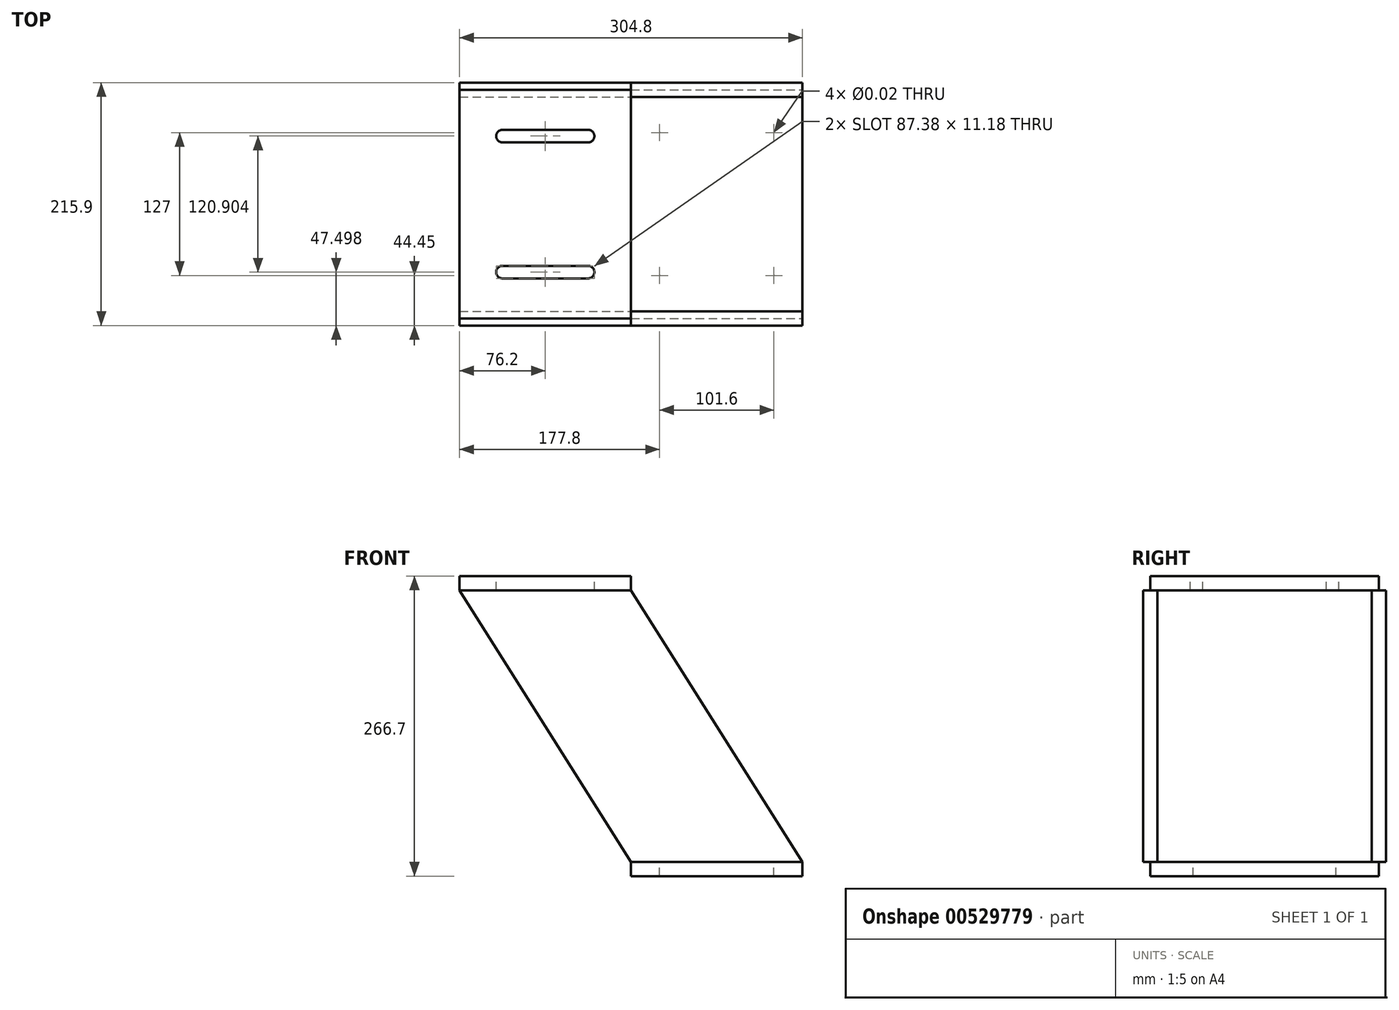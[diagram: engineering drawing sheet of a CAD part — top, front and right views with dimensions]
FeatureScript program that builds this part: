
annotation { "Feature Type Name" : "Feature", "Feature Type Description" : "" }
export const myFeature = defineFeature(function(context is Context, id is Id, definition is map)
    precondition{}
    {
        {
            var Q0;
            Q0=qCreatedBy(makeId("Top.planeOp"),FACE);
            var sketch = newSketch(context, id + "F0", { "sketchPlane" : qUnion([Q0])});
            skLineSegment(sketch, "E0.bottom", {"start": v(-76.2, 101.6) * mm, "end": v(76.2, 101.6) * mm});
            skLineSegment(sketch, "E0.top", {"start": v(-76.2, -101.6) * mm, "end": v(76.2, -101.6) * mm});
            skLineSegment(sketch, "E0.left", {"start": v(-76.2, 101.6) * mm, "end": v(-76.2, -101.6) * mm});
            skLineSegment(sketch, "E0.right", {"start": v(76.2, 101.6) * mm, "end": v(76.2, -101.6) * mm});
            skPoint(sketch, "E0.middle", {"position": v(0, 0) * mm});
            skSolve(sketch);
        }
        {
            var Q0;
            Q0 = qSketchRegion(id + "F0", true);
            extrude(context, id + "F1", {"entities" : qUnion([Q0]), "depth" : 12.7 * mm, "offsetDistance" : 25.4 * mm});
        }
        {
            var Q0;
            Q0=makeQuery(id+"F1.opExtrude","CAP_FACE",FACE,{"disambiguationData":[OSD([sQuery(id+"F0.wireOp",EDGE,"E0.bottom"),sQuery(id+"F0.wireOp",EDGE,"E0.top"),sQuery(id+"F0.wireOp",EDGE,"E0.left"),sQuery(id+"F0.wireOp",EDGE,"E0.right")])],"isStart":false});
            var sketch = newSketch(context, id + "F2", { "sketchPlane" : qUnion([Q0])});
            skLineSegment(sketch, "E1", {"start": v(-132.32, 0) * mm, "end": v(123.37, 0) * mm, "construction": true});
            skLineSegment(sketch, "E2", {"start": v(0, 144.95) * mm, "end": v(0, -143.32) * mm, "construction": true});
            skLineSegment(sketch, "E3.0", {"start": v(-132.32, -63.5) * mm, "end": v(123.37, -63.5) * mm, "construction": true});
            skLineSegment(sketch, "E4.0", {"start": v(-50.8, 144.95) * mm, "end": v(-50.8, -143.32) * mm, "construction": true});
            skPoint(sketch, "E5", {"position": v(-50.8, -63.5) * mm});
            skPoint(sketch, "E6.MirrorP", {"position": v(-50.8, 63.5) * mm});
            skPoint(sketch, "E7.MirrorP", {"position": v(50.8, 63.5) * mm});
            skPoint(sketch, "E8.MirrorP", {"position": v(50.8, -63.5) * mm});
            skSolve(sketch);
        }
        {
            var Q0;
            Q0=sQuery(id+"F2.wireOp",VERTEX,"E6.MirrorP");
            var Q1;
            Q1=sQuery(id+"F2.wireOp",VERTEX,"E7.MirrorP");
            var Q2;
            Q2=sQuery(id+"F2.wireOp",VERTEX,"E5");
            var Q3;
            Q3=sQuery(id+"F2.wireOp",VERTEX,"E8.MirrorP");
            var Q4;
            Q4=makeQuery(id+"F1.opExtrude","SWEPT_BODY",BODY,{"disambiguationData":[OSD([sQuery(id+"F0.wireOp",EDGE,"E0.bottom"),sQuery(id+"F0.wireOp",EDGE,"E0.top"),sQuery(id+"F0.wireOp",EDGE,"E0.left"),sQuery(id+"F0.wireOp",EDGE,"E0.right")])]});
            hole(context, id + "F3", {"style" : HoleStyle.SIMPLE, "endStyle" : HoleEndStyle.THROUGH, "standardTappedOrClearance" : lookupTablePath({ "standard" : "ANSI", "size" : "9/16 (0.56)", "type" : "Drilled" }), "standardBlindInLast" : lookupTablePath({ "standard" : "ANSI", "size" : "9/16", "type" : "Drilled" }), "holeDiameter" : 9 / 406.4 * mm, "isTappedThrough" : true, "tappedDepth" : 9.66 * mm, "tapClearance" : 3, "locations" : qUnion([Q0, Q1, Q2, Q3]), "scope" : qUnion([Q4])});
        }
        {
            var Q0;
            Q0=makeQuery(id+"F1.opExtrude","CAP_FACE",FACE,{"disambiguationData":[OSD([sQuery(id+"F0.wireOp",EDGE,"E0.bottom"),sQuery(id+"F0.wireOp",EDGE,"E0.top"),sQuery(id+"F0.wireOp",EDGE,"E0.left"),sQuery(id+"F0.wireOp",EDGE,"E0.right")])],"isStart":true});
            cPlane(context, id + "F4", {"entities" : qUnion([Q0]), "cplaneType" : CPlaneType.OFFSET, "offset" : 266.7 * mm, "oppositeDirection" : true, "width" : 152.4 * mm, "height" : 152.4 * mm});
        }
        {
            var Q0;
            Q0=qCreatedBy(id+"F4.planeOp",FACE);
            var sketch = newSketch(context, id + "F5", { "sketchPlane" : qUnion([Q0])});
            skLineSegment(sketch, "E9", {"start": v(0, -161.83) * mm, "end": v(0, 162.48) * mm, "construction": true});
            skLineSegment(sketch, "E10", {"start": v(170.54, 0) * mm, "end": v(-318.83, 0) * mm, "construction": true});
            skLineSegment(sketch, "E11.0", {"start": v(-152.4, -161.83) * mm, "end": v(-152.4, 162.48) * mm, "construction": true});
            skLineSegment(sketch, "E12.0", {"start": v(-76.2, -101.6) * mm, "end": v(76.2, -101.6) * mm, "construction": true});
            skLineSegment(sketch, "E13.0", {"start": v(-76.2, 101.6) * mm, "end": v(76.2, 101.6) * mm, "construction": true});
            skLineSegment(sketch, "E14.bottom", {"start": v(-228.6, -101.6) * mm, "end": v(-76.2, -101.6) * mm});
            skLineSegment(sketch, "E14.top", {"start": v(-228.6, 101.6) * mm, "end": v(-76.2, 101.6) * mm});
            skLineSegment(sketch, "E14.left", {"start": v(-228.6, -101.6) * mm, "end": v(-228.6, 101.6) * mm});
            skLineSegment(sketch, "E14.right", {"start": v(-76.2, -101.6) * mm, "end": v(-76.2, 101.6) * mm});
            skPoint(sketch, "E14.middle", {"position": v(-152.4, 0) * mm});
            skSolve(sketch);
        }
        {
            var Q0;
            Q0 = qSketchRegion(id + "F5", true);
            extrude(context, id + "F6", {"entities" : qUnion([Q0]), "depth" : 12.7 * mm, "offsetDistance" : 25.4 * mm});
        }
        {
            var Q0;
            Q0=makeQuery(id+"F6.opExtrude","CAP_FACE",FACE,{"disambiguationData":[OSD([sQuery(id+"F5.wireOp",EDGE,"E14.bottom"),sQuery(id+"F5.wireOp",EDGE,"E14.top"),sQuery(id+"F5.wireOp",EDGE,"E14.left"),sQuery(id+"F5.wireOp",EDGE,"E14.right")])],"isStart":true});
            var sketch = newSketch(context, id + "F7", { "sketchPlane" : qUnion([Q0])});
            skLineSegment(sketch, "E15", {"start": v(-152.4, 101.6) * mm, "end": v(-152.4, -101.6) * mm, "construction": true});
            skLineSegment(sketch, "E16", {"start": v(-228.6, 0) * mm, "end": v(-76.2, 0) * mm, "construction": true});
            skLineSegment(sketch, "E17.0", {"start": v(-190.5, -60.45) * mm, "end": v(-114.3, -60.45) * mm});
            skLineSegment(sketch, "E18.0", {"start": v(-190.5, 101.6) * mm, "end": v(-190.5, -101.6) * mm, "construction": true});
            skLineSegment(sketch, "E19.0", {"start": v(-114.3, 101.6) * mm, "end": v(-114.3, -101.6) * mm, "construction": true});
            skArc(sketch, "E20.0.startCap", {"start": v(-190.5, -66.04) * mm, "mid": v(-196.09, -60.45) * mm, "end": v(-190.5, -54.86) * mm});
            skArc(sketch, "E20.0.endCap", {"start": v(-114.3, -54.86) * mm, "mid": v(-108.71, -60.45) * mm, "end": v(-114.3, -66.04) * mm});
            skLineSegment(sketch, "E20.0.left", {"start": v(-190.5, -54.86) * mm, "end": v(-114.3, -54.86) * mm});
            skLineSegment(sketch, "E20.0.right", {"start": v(-190.5, -66.04) * mm, "end": v(-114.3, -66.04) * mm});
            skArc(sketch, "E21.MirrorCS", {"start": v(-114.3, 54.86) * mm, "mid": v(-108.71, 60.45) * mm, "end": v(-114.3, 66.04) * mm});
            skLineSegment(sketch, "E22.MirrorCS", {"start": v(-190.5, 66.04) * mm, "end": v(-114.3, 66.04) * mm});
            skLineSegment(sketch, "E23.MirrorCS", {"start": v(-190.5, 54.86) * mm, "end": v(-114.3, 54.86) * mm});
            skArc(sketch, "E24.MirrorCS", {"start": v(-190.5, 66.04) * mm, "mid": v(-196.09, 60.45) * mm, "end": v(-190.5, 54.86) * mm});
            skLineSegment(sketch, "E25.MirrorCS", {"start": v(-190.5, 60.45) * mm, "end": v(-114.3, 60.45) * mm});
            skSolve(sketch);
        }
        {
            var Q0;
            Q0 = qSketchRegion(id + "F7", true);
            extrude(context, id + "F8", {"entities" : qUnion([Q0]), "operationType" : NewBodyOperationType.REMOVE, "endBound" : BoundingType.THROUGH_ALL, "oppositeDirection" : true, "depth" : 25.4 * mm, "offsetDistance" : 25.4 * mm});
        }
        {
            var Q0;
            Q0=makeQuery(id+"F1.opExtrude","SWEPT_FACE",FACE,{"disambiguationData":[OSD([sQuery(id+"F0.wireOp",EDGE,"E0.top")])]});
            var sketch = newSketch(context, id + "F9", { "sketchPlane" : qUnion([Q0])});
            skLineSegment(sketch, "E26.0", {"start": v(-228.6, 254) * mm, "end": v(-76.2, 254) * mm});
            skLineSegment(sketch, "E27.0", {"start": v(-76.2, 12.7) * mm, "end": v(76.2, 12.7) * mm});
            skLineSegment(sketch, "E28", {"start": v(-228.6, 254) * mm, "end": v(-76.2, 12.7) * mm});
            skLineSegment(sketch, "E29", {"start": v(-76.2, 254) * mm, "end": v(76.2, 12.7) * mm});
            skSolve(sketch);
        }
        {
            var Q0;
            Q0 = qSketchRegion(id + "F9", true);
            extrude(context, id + "F10", {"entities" : qUnion([Q0]), "endBound" : BoundingType.SYMMETRIC, "depth" : 12.7 * mm, "offsetDistance" : 25.4 * mm});
        }
        {
            var Q0;
            Q0=makeQuery(id+"F10.opExtrude","SWEPT_BODY",BODY,{"disambiguationData":[OSD([sQuery(id+"F9.wireOp",EDGE,"E26.0"),sQuery(id+"F9.wireOp",EDGE,"E27.0"),sQuery(id+"F9.wireOp",EDGE,"E28"),sQuery(id+"F9.wireOp",EDGE,"E29")])]});
            var Q1;
            Q1=qCreatedBy(makeId("Front.planeOp"),FACE);
            mirror(context, id + "F11", {"entities" : qUnion([Q0]), "mirrorPlane" : qUnion([Q1])});
        }
    });
